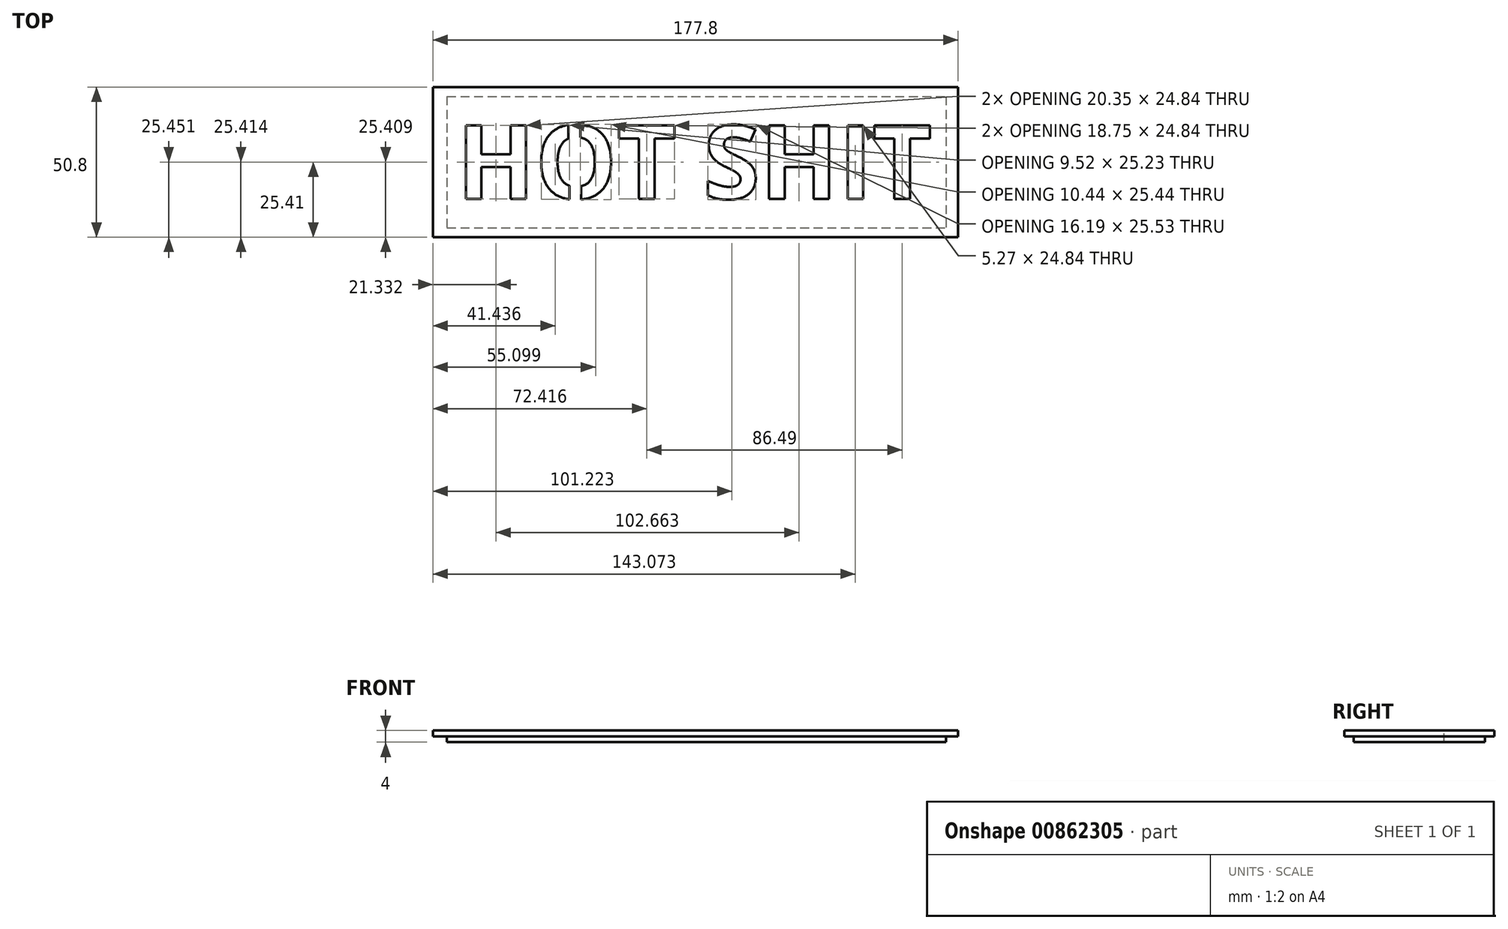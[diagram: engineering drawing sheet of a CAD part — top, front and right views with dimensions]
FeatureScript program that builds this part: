
annotation { "Feature Type Name" : "Feature", "Feature Type Description" : "" }
export const myFeature = defineFeature(function(context is Context, id is Id, definition is map)
    precondition{}
    {
        {
            var Q0;
            Q0=qCreatedBy(makeId("Top.planeOp"),FACE);
            var sketch = newSketch(context, id + "F0", { "sketchPlane" : qUnion([Q0])});
            skLineSegment(sketch, "E0.bottom", {"start": v(-86.65, 12.76) * mm, "end": v(91.15, 12.76) * mm});
            skLineSegment(sketch, "E0.top", {"start": v(-86.65, -38.04) * mm, "end": v(91.15, -38.04) * mm});
            skLineSegment(sketch, "E0.left", {"start": v(-86.65, 12.76) * mm, "end": v(-86.65, -38.04) * mm});
            skLineSegment(sketch, "E0.right", {"start": v(91.15, 12.76) * mm, "end": v(91.15, -38.04) * mm});
            skLineSegment(sketch, "E1.bottom", {"start": v(-81.88, 9.6) * mm, "end": v(87.12, 9.6) * mm});
            skLineSegment(sketch, "E1.top", {"start": v(-81.88, -34.85) * mm, "end": v(87.12, -34.85) * mm});
            skLineSegment(sketch, "E1.left", {"start": v(-81.88, 9.6) * mm, "end": v(-81.88, -34.85) * mm});
            skLineSegment(sketch, "E1.right", {"start": v(87.12, 9.6) * mm, "end": v(87.12, -34.85) * mm});
            skText(sketch, "E2", { "text": "HOT SHIT", "fontName": "OpenSans-Bold.ttf"});
            skLineSegment(sketch, "E3", {"start": v(-40.76, 0) * mm, "end": v(-40.76, -4.74) * mm});
            skLineSegment(sketch, "E4", {"start": v(-36.76, -4.94) * mm, "end": v(-36.76, 0) * mm});
            skLineSegment(sketch, "E5", {"start": v(-40.76, 0) * mm, "end": v(-40.76, 1.39) * mm});
            skLineSegment(sketch, "E6", {"start": v(-40.76, 1.39) * mm, "end": v(-36.87, 1.39) * mm});
            skLineSegment(sketch, "E7", {"start": v(-36.87, 1.39) * mm, "end": v(-36.76, 0) * mm});
            skLineSegment(sketch, "E8", {"start": v(-36.76, -4.94) * mm, "end": v(-40.76, -4.74) * mm});
            skLineSegment(sketch, "E9", {"start": v(-40.45, -25.05) * mm, "end": v(-36.45, -25.05) * mm});
            skLineSegment(sketch, "E10", {"start": v(-36.45, -18.95) * mm, "end": v(-40.45, -18.95) * mm});
            skLineSegment(sketch, "E11", {"start": v(-40.45, -25.95) * mm, "end": v(-36.4, -25.95) * mm});
            skLineSegment(sketch, "E12", {"start": v(-36.4, -25.95) * mm, "end": v(-36.45, -18.95) * mm});
            skLineSegment(sketch, "E13", {"start": v(-40.45, -18.95) * mm, "end": v(-40.45, -25.95) * mm});
            const initialGuessF0  = {"E2": [-0.07862, -0.02505, 1, 0, 0.02505]};
            skSetInitialGuess(sketch, initialGuessF0);
            skSolve(sketch);
        }
        {
            var Q0;
            Q0=makeQuery(id+"F0.imprint","IMPRINT",FACE,{"disambiguationData":[TD([[makeQuery(id+"F0.imprint","IMPRINT",EDGE,{"derivedFrom":sQuery(id+"F0.wireOp",EDGE,"E1.bottom")}),-1.0]])]});
            var Q1;
            {var subQ5=sQuery(id+"F0.wireOp",EDGE,"E2.sketch_text.stroke-18");var subQ6=sQuery(id+"F0.wireOp",EDGE,"E2.sketch_text.stroke-17");var subQ7=makeQuery(id+"F0.imprint","INTERSECT",VERTEX,{"derivedFrom":[subQ6,subQ5]});Q1=makeQuery(id+"F0.imprint","IMPRINT",FACE,{"disambiguationData":[TD([[makeQuery(id+"F0.imprint","IMPRINT",EDGE,{"disambiguationData":[TD([[subQ7,1.0]])],"derivedFrom":subQ6}),-1.0]])]});}
            var Q2;
            {var subQ0=sQuery(id+"F0.wireOp",EDGE,"E8");Q2=makeQuery(id+"F0.imprint","IMPRINT",FACE,{"disambiguationData":[TD([[makeQuery(id+"F0.imprint","IMPRINT",EDGE,{"derivedFrom":subQ0}),-1.0]])]});}
            var Q3;
            {var subQ13=sQuery(id+"F0.wireOp",EDGE,"E2.sketch_text.stroke-20");Q3=makeQuery(id+"F0.imprint","IMPRINT",FACE,{"disambiguationData":[TD([[makeQuery(id+"F0.imprint","IMPRINT",EDGE,{"derivedFrom":subQ13}),1.0]])]});}
            var Q4;
            {var subQ0=sQuery(id+"F0.wireOp",EDGE,"E6");Q4=makeQuery(id+"F0.imprint","IMPRINT",FACE,{"disambiguationData":[TD([[makeQuery(id+"F0.imprint","IMPRINT",EDGE,{"derivedFrom":subQ0}),-1.0]])]});}
            var Q5;
            {var subQ1=sQuery(id+"F0.wireOp",EDGE,"E10");Q5=makeQuery(id+"F0.imprint","IMPRINT",FACE,{"disambiguationData":[TD([[makeQuery(id+"F0.imprint","IMPRINT",EDGE,{"derivedFrom":subQ1}),1.0]])]});}
            var Q6;
            {var subQ5=sQuery(id+"F0.wireOp",EDGE,"E13");var subQ12=makeQuery(id+"F0.imprint","IMPRINT",VERTEX,{"derivedFrom":subQ5});Q6=makeQuery(id+"F0.imprint","IMPRINT",FACE,{"disambiguationData":[TD([[makeQuery(id+"F0.imprint","IMPRINT",EDGE,{"disambiguationData":[TD([[subQ12,1.0]])],"derivedFrom":subQ5}),1.0]])]});}
            var Q7;
            {var subQ1=sQuery(id+"F0.wireOp",EDGE,"E11");Q7=makeQuery(id+"F0.imprint","IMPRINT",FACE,{"disambiguationData":[TD([[makeQuery(id+"F0.imprint","IMPRINT",EDGE,{"derivedFrom":subQ1}),1.0]])]});}
            extrude(context, id + "F1", {"entities" : qUnion([Q0, Q1, Q2, Q3, Q4, Q5, Q6, Q7]), "oppositeDirection" : true, "depth" : 4 * mm, "offsetDistance" : 25 * mm});
        }
        {
            var Q0;
            Q0=makeQuery(id+"F0.imprint","IMPRINT",FACE,{"disambiguationData":[TD([[makeQuery(id+"F0.imprint","IMPRINT",EDGE,{"derivedFrom":sQuery(id+"F0.wireOp",EDGE,"E0.bottom")}),-1.0]])]});
            extrude(context, id + "F2", {"entities" : qUnion([Q0]), "operationType" : NewBodyOperationType.ADD, "oppositeDirection" : true, "depth" : 2 * mm, "offsetDistance" : 25 * mm});
        }
    });
